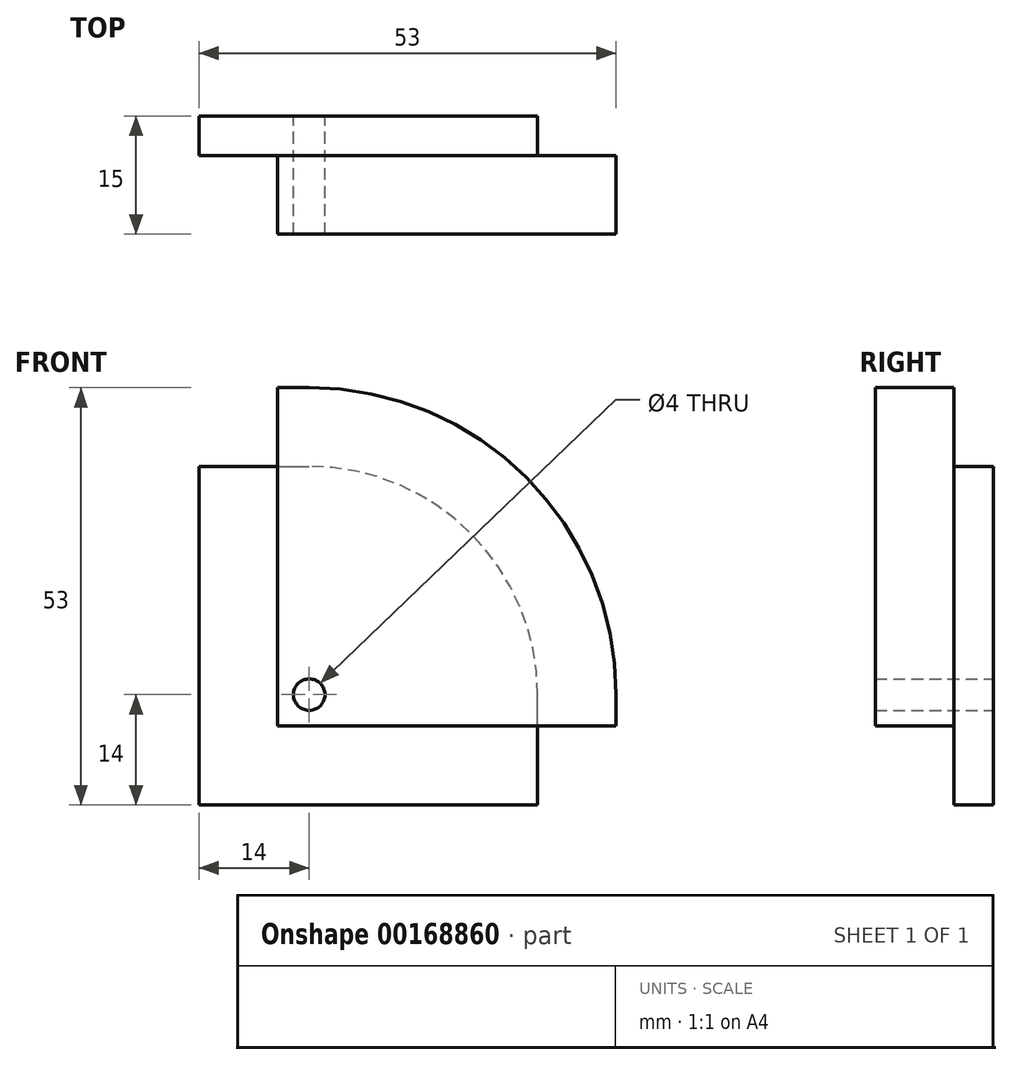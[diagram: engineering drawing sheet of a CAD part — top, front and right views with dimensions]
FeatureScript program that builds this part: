
annotation { "Feature Type Name" : "Feature", "Feature Type Description" : "" }
export const myFeature = defineFeature(function(context is Context, id is Id, definition is map)
    precondition{}
    {
        {
            var Q0;
            Q0=qCreatedBy(makeId("Front.planeOp"),FACE);
            var sketch = newSketch(context, id + "F0", { "sketchPlane" : qUnion([Q0])});
            skLineSegment(sketch, "E0.bottom", {"start": v(0, 0) * mm, "end": v(43, 0) * mm});
            skLineSegment(sketch, "E0.top", {"start": v(0, 43) * mm, "end": v(14, 43) * mm});
            skLineSegment(sketch, "E0.left", {"start": v(0, 0) * mm, "end": v(0, 43) * mm});
            skLineSegment(sketch, "E0.right", {"start": v(43, 0) * mm, "end": v(43, 14) * mm});
            skPoint(sketch, "E1.visualSharp", {"position": v(43, 43) * mm});
            skArc(sketch, "E1.filletArc", {"start": v(43, 14) * mm, "mid": v(34.5, 34.5) * mm, "end": v(14, 43) * mm});
            skLineSegment(sketch, "E2.bottom", {"start": v(10, 10) * mm, "end": v(53, 10) * mm});
            skLineSegment(sketch, "E2.top", {"start": v(10, 53) * mm, "end": v(14, 53) * mm});
            skLineSegment(sketch, "E2.left", {"start": v(10, 10) * mm, "end": v(10, 53) * mm});
            skLineSegment(sketch, "E2.right", {"start": v(53, 10) * mm, "end": v(53, 14) * mm});
            skPoint(sketch, "E3.visualSharp", {"position": v(53, 53) * mm});
            skArc(sketch, "E3.filletArc", {"start": v(53, 14) * mm, "mid": v(41.58, 41.58) * mm, "end": v(14, 53) * mm});
            skCircle(sketch, "E4", {"center": v(14, 14) * mm, "radius": 2 * mm});
            skSolve(sketch);
        }
        {
            var Q0;
            {var subQ1=sQuery(id+"F0.wireOp",EDGE,"E0.bottom");Q0=makeQuery(id+"F0.imprint","IMPRINT",FACE,{"disambiguationData":[TD([[makeQuery(id+"F0.imprint","IMPRINT",EDGE,{"derivedFrom":subQ1}),1.0]])]});}
            extrude(context, id + "F1", {"entities" : qUnion([Q0]), "oppositeDirection" : true, "depth" : 5 * mm});
        }
        {
            var Q0;
            {var subQ5=sQuery(id+"F0.wireOp",EDGE,"E1.filletArc");Q0=makeQuery(id+"F0.imprint","IMPRINT",FACE,{"disambiguationData":[TD([[makeQuery(id+"F0.imprint","IMPRINT",EDGE,{"derivedFrom":subQ5}),1.0]])]});}
            extrude(context, id + "F2", {"entities" : qUnion([Q0]), "operationType" : NewBodyOperationType.ADD, "depth" : 10 * mm, "hasSecondDirection" : true, "secondDirectionOppositeDirection" : true, "secondDirectionDepth" : 5 * mm});
        }
        {
            var Q0;
            {var subQ4=sQuery(id+"F0.wireOp",EDGE,"E1.filletArc");Q0=makeQuery(id+"F0.imprint","IMPRINT",FACE,{"disambiguationData":[TD([[makeQuery(id+"F0.imprint","IMPRINT",EDGE,{"derivedFrom":subQ4}),-1.0]])]});}
            extrude(context, id + "F3", {"entities" : qUnion([Q0]), "operationType" : NewBodyOperationType.ADD, "depth" : 10 * mm});
        }
    });
